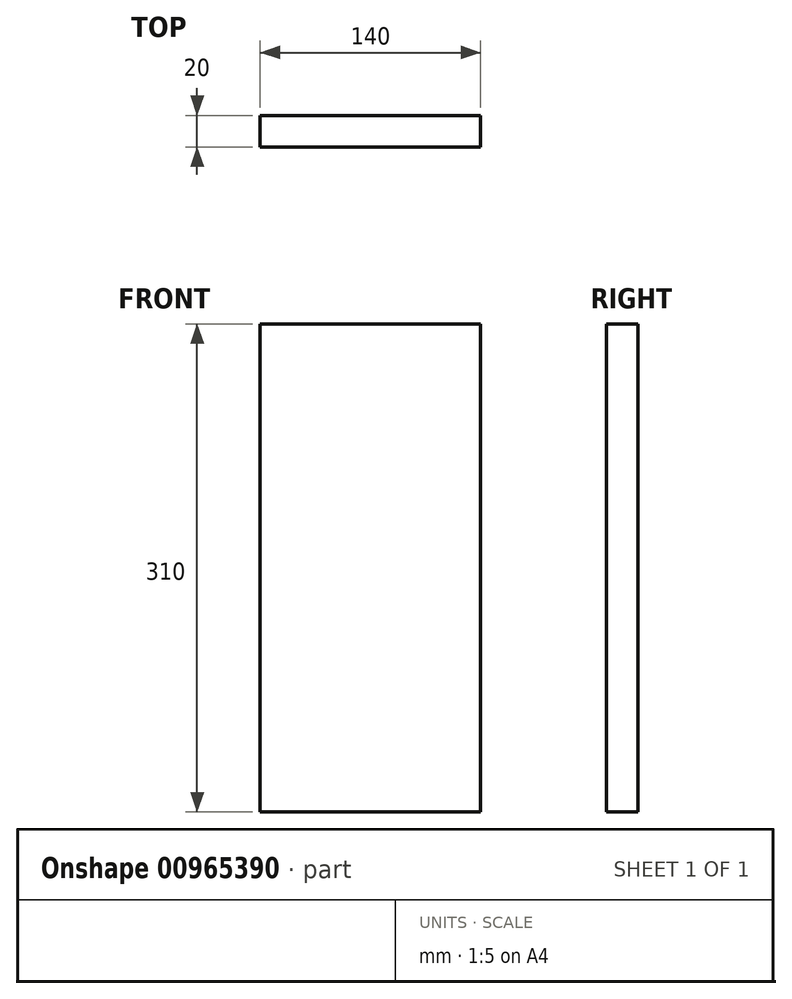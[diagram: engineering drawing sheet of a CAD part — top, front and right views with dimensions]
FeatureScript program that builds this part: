
annotation { "Feature Type Name" : "Feature", "Feature Type Description" : "" }
export const myFeature = defineFeature(function(context is Context, id is Id, definition is map)
    precondition{}
    {
        {
            var Q0;
            Q0=qCreatedBy(makeId("Top.planeOp"),FACE);
            var sketch = newSketch(context, id + "F0", { "sketchPlane" : qUnion([Q0])});
            skLineSegment(sketch, "E0.bottom", {"start": v(70, 10) * mm, "end": v(-70, 10) * mm});
            skLineSegment(sketch, "E0.top", {"start": v(70, -10) * mm, "end": v(-70, -10) * mm});
            skLineSegment(sketch, "E0.left", {"start": v(70, 10) * mm, "end": v(70, -10) * mm});
            skLineSegment(sketch, "E0.right", {"start": v(-70, 10) * mm, "end": v(-70, -10) * mm});
            skPoint(sketch, "E0.middle", {"position": v(0, 0) * mm});
            skSolve(sketch);
        }
        {
            var Q0;
            Q0=makeQuery(id+"F0.imprint","IMPRINT",FACE,{"disambiguationData":[TD([[makeQuery(id+"F0.imprint","IMPRINT",EDGE,{"derivedFrom":sQuery(id+"F0.wireOp",EDGE,"E0.bottom")}),1.0]])]});
            extrude(context, id + "F1", {"entities" : qUnion([Q0]), "depth" : 310 * mm, "offsetDistance" : 25 * mm});
        }
    });
